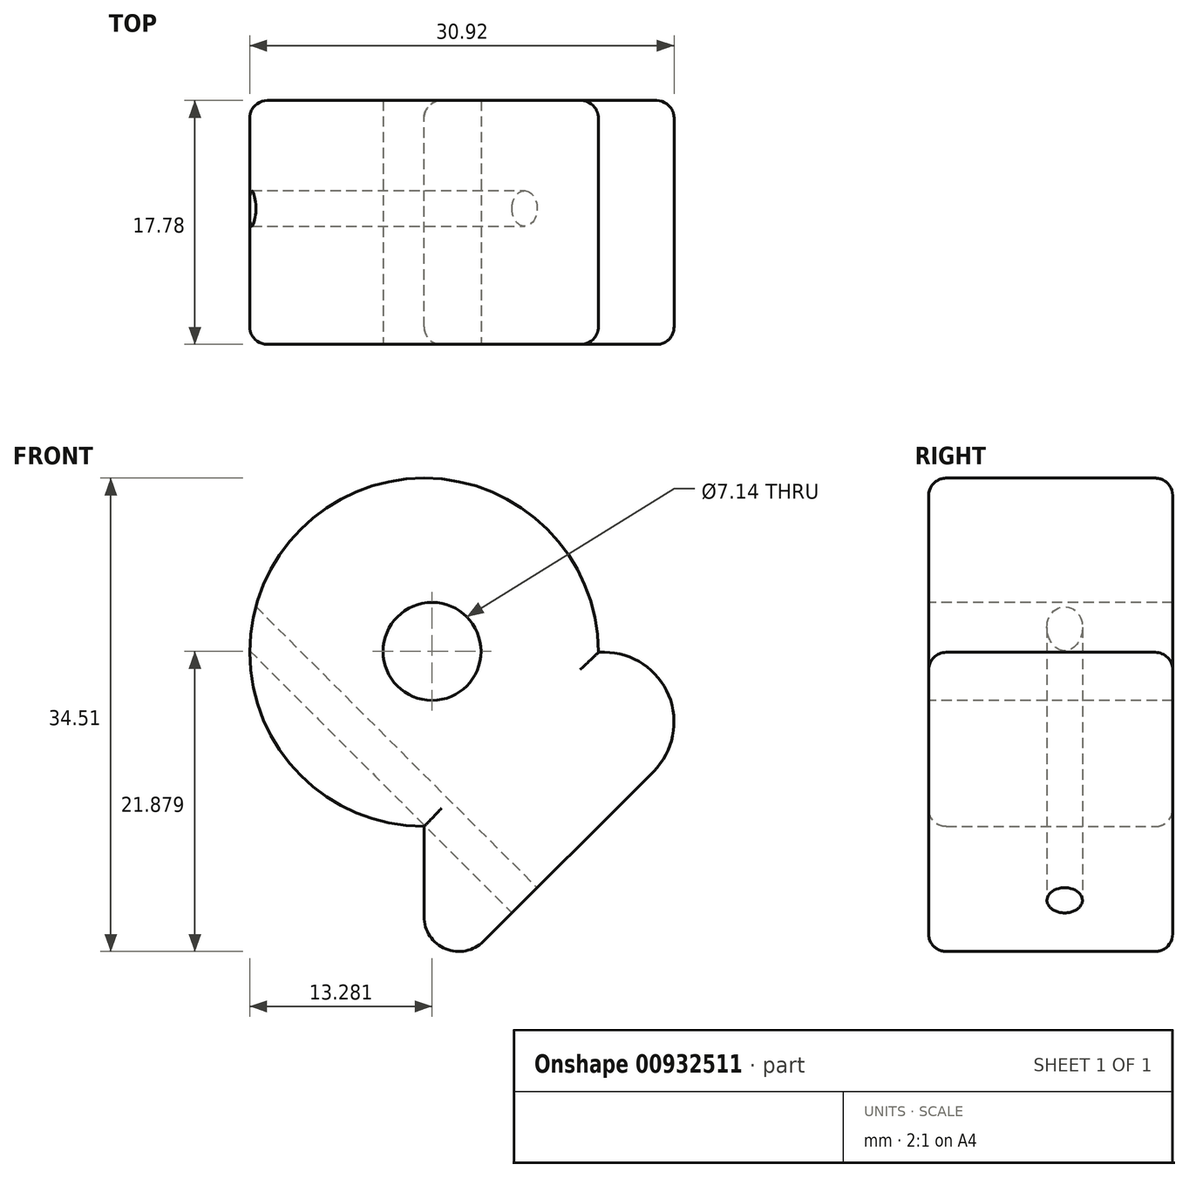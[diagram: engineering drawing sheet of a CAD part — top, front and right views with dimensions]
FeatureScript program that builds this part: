
annotation { "Feature Type Name" : "Feature", "Feature Type Description" : "" }
export const myFeature = defineFeature(function(context is Context, id is Id, definition is map)
    precondition{}
    {
        {
            var Q0;
            Q0=qCreatedBy(makeId("Front.planeOp"),FACE);
            var sketch = newSketch(context, id + "F0", { "sketchPlane" : qUnion([Q0])});
            skCircle(sketch, "E0", {"center": v(-47.95, 35.77) * mm, "radius": 12.7 * mm});
            skLineSegment(sketch, "E1", {"start": v(-47.95, 35.77) * mm, "end": v(-47.95, 10.37) * mm});
            skLineSegment(sketch, "E2", {"start": v(-47.95, 35.77) * mm, "end": v(-22.55, 35.77) * mm});
            skLineSegment(sketch, "E3", {"start": v(-47.95, 10.37) * mm, "end": v(-22.55, 35.77) * mm});
            skSolve(sketch);
        }
        {
            var Q0;
            {var subQ5=sQuery(id+"F0.wireOp",EDGE,"E3");Q0=makeQuery(id+"F0.imprint","IMPRINT",FACE,{"disambiguationData":[TD([[makeQuery(id+"F0.imprint","IMPRINT",EDGE,{"derivedFrom":subQ5}),1.0]])]});}
            var Q1;
            {var subQ0=sQuery(id+"F0.wireOp",EDGE,"E1");var subQ1=sQuery(id+"F0.wireOp",EDGE,"E0");var subQ2=makeQuery(id+"F0.imprint","INTERSECT",VERTEX,{"derivedFrom":[subQ1,subQ0]});Q1=makeQuery(id+"F0.imprint","IMPRINT",FACE,{"disambiguationData":[TD([[makeQuery(id+"F0.imprint","IMPRINT",EDGE,{"disambiguationData":[TD([[subQ2,1.0]])],"derivedFrom":subQ1}),1.0]])]});}
            var Q2;
            {var subQ0=sQuery(id+"F0.wireOp",EDGE,"E1");var subQ1=sQuery(id+"F0.wireOp",EDGE,"E0");var subQ2=makeQuery(id+"F0.imprint","INTERSECT",VERTEX,{"derivedFrom":[subQ1,subQ0]});Q2=makeQuery(id+"F0.imprint","IMPRINT",FACE,{"disambiguationData":[TD([[makeQuery(id+"F0.imprint","IMPRINT",EDGE,{"disambiguationData":[TD([[subQ2,-1.0]])],"derivedFrom":subQ1}),1.0]])]});}
            extrude(context, id + "F1", {"entities" : qUnion([Q0, Q1, Q2]), "depth" : 17.78 * mm, "offsetDistance" : 25.4 * mm});
        }
        {
            var Q0;
            Q0=makeQuery(id+"F1.opExtrude","SWEPT_EDGE",EDGE,{"disambiguationData":[OSD([sQuery(id+"F0.wireOp",EDGE,"E2"),sQuery(id+"F0.wireOp",EDGE,"E3")])]});
            fillet(context, id + "F2", {"entities" : qUnion([Q0]), "radius" : 5.08 * mm, "tangentPropagation" : true, "allowEdgeOverflow" : false});
        }
        {
            var Q0;
            Q0=makeQuery(id+"F1.opExtrude","SWEPT_EDGE",EDGE,{"disambiguationData":[OSD([sQuery(id+"F0.wireOp",EDGE,"E1"),sQuery(id+"F0.wireOp",EDGE,"E3")])]});
            fillet(context, id + "F3", {"entities" : qUnion([Q0]), "radius" : 2.54 * mm, "tangentPropagation" : true, "allowEdgeOverflow" : false});
        }
        {
            var Q0;
            Q0=makeQuery(id+"F1.opExtrude","CAP_EDGE",EDGE,{"disambiguationData":[OSD([sQuery(id+"F0.wireOp",EDGE,"E0")])],"isStart":false});
            var Q1;
            {var subQ0=sQuery(id+"F0.wireOp",EDGE,"E3");var subQ1=sQuery(id+"F0.wireOp",EDGE,"E2");Q1=makeQuery(id+"F2.opFillet","BLEND_EDGE",EDGE,{"blendedFrom":[makeQuery(id+"F1.opExtrude","SWEPT_EDGE",EDGE,{"disambiguationData":[OSD([subQ1,subQ0])]}),makeQuery(id+"F1.opExtrude","CAP_FACE",FACE,{"disambiguationData":[OSD([sQuery(id+"F0.wireOp",EDGE,"E0"),sQuery(id+"F0.wireOp",EDGE,"E1"),subQ1,subQ0])],"isStart":false})],"blendedInto":[makeQuery(id+"F1.opExtrude","CAP_FACE",FACE,{"disambiguationData":[OSD([sQuery(id+"F0.wireOp",EDGE,"E0"),sQuery(id+"F0.wireOp",EDGE,"E1"),subQ1,subQ0])],"isStart":false})]});}
            var Q2;
            Q2=makeQuery(id+"F1.opExtrude","CAP_EDGE",EDGE,{"disambiguationData":[OSD([sQuery(id+"F0.wireOp",EDGE,"E3")])],"isStart":false});
            var Q3;
            Q3=makeQuery(id+"F1.opExtrude","CAP_FACE",FACE,{"disambiguationData":[OSD([sQuery(id+"F0.wireOp",EDGE,"E0"),sQuery(id+"F0.wireOp",EDGE,"E1"),sQuery(id+"F0.wireOp",EDGE,"E2"),sQuery(id+"F0.wireOp",EDGE,"E3")])],"isStart":false});
            fillet(context, id + "F4", {"entities" : qUnion([Q0, Q1, Q2, Q3]), "radius" : 1.27 * mm, "tangentPropagation" : true, "allowEdgeOverflow" : false});
        }
        {
            var Q0;
            Q0=makeQuery(id+"F1.opExtrude","CAP_EDGE",EDGE,{"disambiguationData":[OSD([sQuery(id+"F0.wireOp",EDGE,"E0")])],"isStart":true});
            fillet(context, id + "F5", {"entities" : qUnion([Q0]), "radius" : 1.27 * mm, "tangentPropagation" : true, "allowEdgeOverflow" : false});
        }
        {
            var Q0;
            Q0=makeQuery(id+"F1.opExtrude","CAP_FACE",FACE,{"disambiguationData":[OSD([sQuery(id+"F0.wireOp",EDGE,"E0"),sQuery(id+"F0.wireOp",EDGE,"E1"),sQuery(id+"F0.wireOp",EDGE,"E2"),sQuery(id+"F0.wireOp",EDGE,"E3")])],"isStart":true});
            fillet(context, id + "F6", {"entities" : qUnion([Q0]), "radius" : 1.27 * mm, "tangentPropagation" : true, "allowEdgeOverflow" : false});
        }
        {
            var Q0;
            Q0=makeQuery(id+"F1.opExtrude","CAP_FACE",FACE,{"disambiguationData":[OSD([sQuery(id+"F0.wireOp",EDGE,"E0"),sQuery(id+"F0.wireOp",EDGE,"E1"),sQuery(id+"F0.wireOp",EDGE,"E2"),sQuery(id+"F0.wireOp",EDGE,"E3")])],"isStart":false});
            cPlane(context, id + "F7", {"entities" : qUnion([Q0]), "cplaneType" : CPlaneType.OFFSET, "offset" : 0 * mm, "width" : 152.4 * mm, "height" : 152.4 * mm});
        }
        {
            var Q0;
            Q0=qCreatedBy(id+"F7.planeOp",FACE);
            var sketch = newSketch(context, id + "F8", { "sketchPlane" : qUnion([Q0])});
            skLineSegment(sketch, "E4", {"start": v(-47.37, 35.84) * mm, "end": v(-42.32, 40.14) * mm});
            skLineSegment(sketch, "E5", {"start": v(-47.37, 35.84) * mm, "end": v(-42.44, 30.05) * mm});
            skSolve(sketch);
        }
        {
            var Q0;
            Q0=sQuery(id+"F8.wireOp",VERTEX,"E4.start");
            var Q1;
            Q1=makeQuery(id+"F1.opExtrude","SWEPT_BODY",BODY,{"disambiguationData":[OSD([sQuery(id+"F0.wireOp",EDGE,"E0"),sQuery(id+"F0.wireOp",EDGE,"E1"),sQuery(id+"F0.wireOp",EDGE,"E2"),sQuery(id+"F0.wireOp",EDGE,"E3")])]});
            hole(context, id + "F9", {"style" : HoleStyle.SIMPLE, "endStyle" : HoleEndStyle.BLIND, "standardTappedOrClearance" : lookupTablePath({ "fit" : "Normal (ASME)", "standard" : "ANSI", "size" : "1/4", "type" : "Clearance" }), "standardBlindInLast" : lookupTablePath({ "fit" : "Normal", "standard" : "ANSI", "engagement" : "75%", "pitch" : "20 tpi", "size" : "1/4", "type" : "Clearance & tapped" }), "holeDiameter" : 7.14 * mm, "majorDiameter" : 6.35 * mm, "holeDepth" : 17.78 * mm, "isTappedThrough" : true, "tappedDepth" : 12.7 * mm, "tapClearance" : 3, "startFromSketch" : true, "locations" : qUnion([Q0]), "scope" : qUnion([Q1])});
        }
        {
            var Q0;
            Q0=makeQuery(id+"F1.opExtrude","SWEPT_FACE",FACE,{"disambiguationData":[OSD([sQuery(id+"F0.wireOp",EDGE,"E3")])]});
            cPlane(context, id + "F10", {"entities" : qUnion([Q0]), "cplaneType" : CPlaneType.OFFSET, "offset" : 0 * mm, "width" : 152.4 * mm, "height" : 152.4 * mm});
        }
        {
            var Q0;
            Q0=qCreatedBy(id+"F10.planeOp",FACE);
            var sketch = newSketch(context, id + "F11", { "sketchPlane" : qUnion([Q0])});
            skCircle(sketch, "E6", {"center": v(-7.87, -16.21) * mm, "radius": 1.26 * mm});
            skSolve(sketch);
        }
        {
            var Q0;
            Q0=sQuery(id+"F11.wireOp",VERTEX,"E6.center");
            var Q1;
            Q1=makeQuery(id+"F1.opExtrude","SWEPT_BODY",BODY,{"disambiguationData":[OSD([sQuery(id+"F0.wireOp",EDGE,"E0"),sQuery(id+"F0.wireOp",EDGE,"E1"),sQuery(id+"F0.wireOp",EDGE,"E2"),sQuery(id+"F0.wireOp",EDGE,"E3")])]});
            hole(context, id + "F12", {"style" : HoleStyle.SIMPLE, "endStyle" : HoleEndStyle.BLIND, "standardTappedOrClearance" : lookupTablePath({ "fit" : "Normal (ASME)", "standard" : "ANSI", "size" : "#2", "type" : "Clearance" }), "standardBlindInLast" : lookupTablePath({ "fit" : "Normal", "standard" : "ANSI", "engagement" : "75%", "pitch" : "56 tpi", "size" : "#2", "type" : "Clearance & tapped" }), "holeDiameter" : 2.6 * mm, "majorDiameter" : 6.35 * mm, "holeDepth" : 30.48 * mm, "isTappedThrough" : true, "tappedDepth" : 12.7 * mm, "tapClearance" : 3, "startFromSketch" : true, "locations" : qUnion([Q0]), "scope" : qUnion([Q1])});
        }
    });
